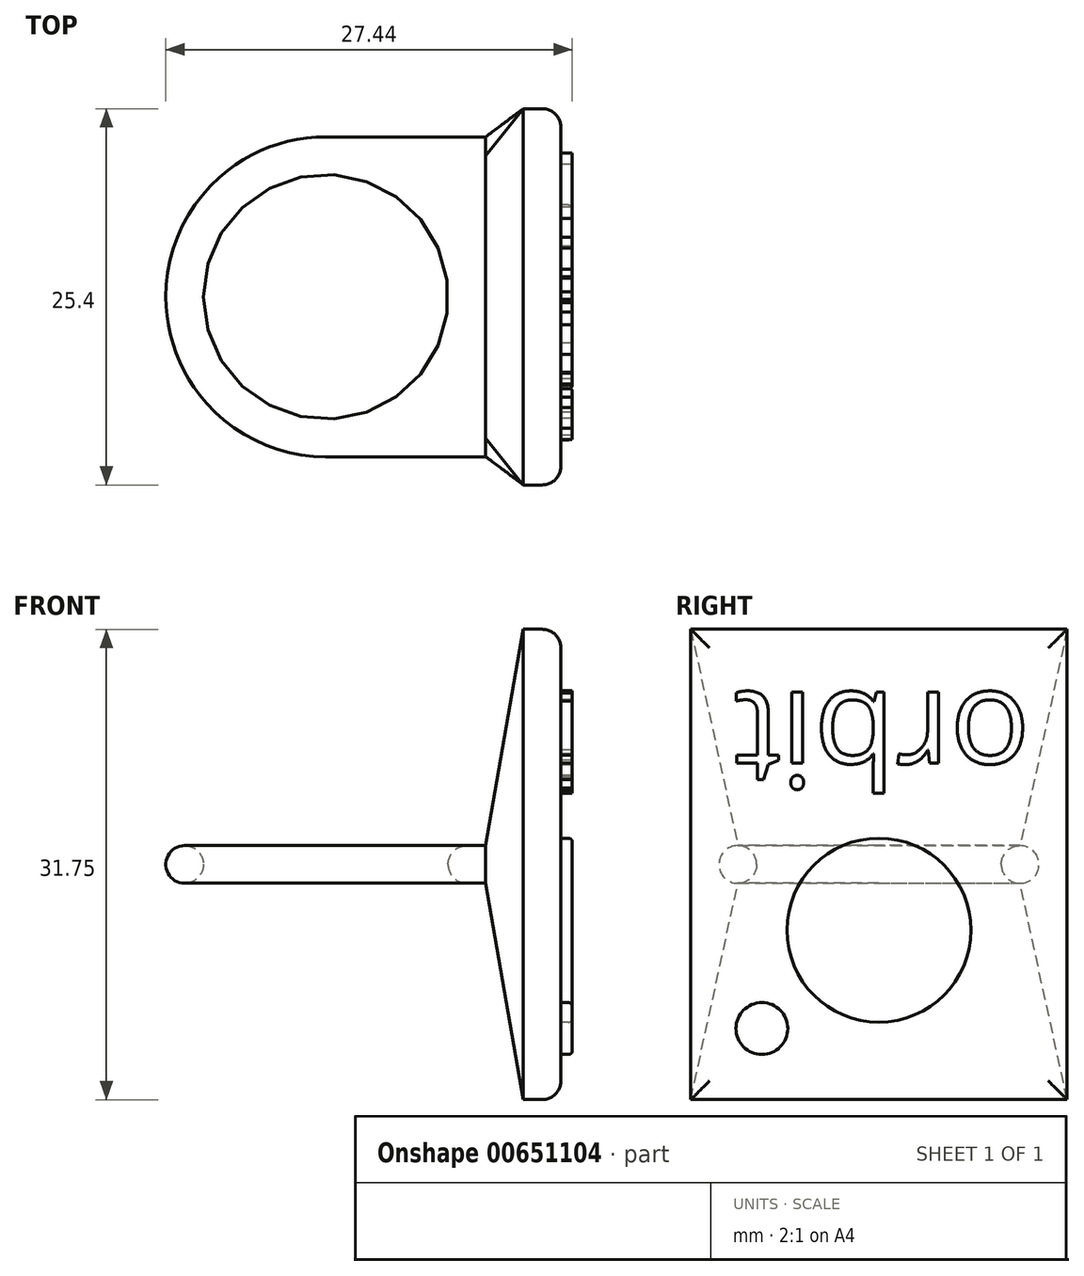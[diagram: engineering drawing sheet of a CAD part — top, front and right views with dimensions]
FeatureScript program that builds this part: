
annotation { "Feature Type Name" : "Feature", "Feature Type Description" : "" }
export const myFeature = defineFeature(function(context is Context, id is Id, definition is map)
    precondition{}
    {
        {
            var Q0;
            Q0=qCreatedBy(makeId("Top.planeOp"),FACE);
            var sketch = newSketch(context, id + "F0", { "sketchPlane" : qUnion([Q0])});
            skCircle(sketch, "E0", {"center": v(0, 0) * mm, "radius": 8.26 * mm});
            skCircle(sketch, "E1.0", {"center": v(0, 0) * mm, "radius": 10.8 * mm});
            skLineSegment(sketch, "E2", {"start": v(0, -10.8) * mm, "end": v(28.84, -10.8) * mm});
            skLineSegment(sketch, "E3", {"start": v(0, 10.8) * mm, "end": v(27.85, 10.8) * mm});
            skLineSegment(sketch, "E4", {"start": v(10.8, 0) * mm, "end": v(10.8, 10.8) * mm});
            skLineSegment(sketch, "E5", {"start": v(10.8, 10.8) * mm, "end": v(10.8, -10.8) * mm});
            skSolve(sketch);
        }
        {
            var Q0;
            Q0=qSketchRegion(id+"F0",true);
            extrude(context, id + "F1", {"entities" : qUnion([Q0]), "depth" : 2.54 * mm, "offsetDistance" : 25.4 * mm});
        }
        {
            var Q0;
            Q0=makeQuery(id+"F1.opExtrude","CAP_EDGE",EDGE,{"disambiguationData":[OSD([sQuery(id+"F0.wireOp",EDGE,"E0")])],"isStart":false});
            var Q1;
            Q1=makeQuery(id+"F1.opExtrude","CAP_EDGE",EDGE,{"disambiguationData":[OSD([sQuery(id+"F0.wireOp",EDGE,"E0")])],"isStart":true});
            var Q2;
            Q2=makeQuery(id+"F1.opExtrude","CAP_EDGE",EDGE,{"disambiguationData":[OSD([sQuery(id+"F0.wireOp",EDGE,"E1.0")])],"isStart":false});
            var Q3;
            Q3=makeQuery(id+"F1.opExtrude","CAP_EDGE",EDGE,{"disambiguationData":[OSD([sQuery(id+"F0.wireOp",EDGE,"E1.0")])],"isStart":true});
            fillet(context, id + "F2", {"entities" : qUnion([Q0, Q1, Q2, Q3]), "radius" : 1.27 * mm, "tangentPropagation" : true, "allowEdgeOverflow" : false});
        }
        {
            var Q0;
            Q0=makeQuery(id+"F1.opExtrude","SWEPT_FACE",FACE,{"disambiguationData":[OSD([sQuery(id+"F0.wireOp",EDGE,"E5")])]});
            cPlane(context, id + "F3", {"entities" : qUnion([Q0]), "cplaneType" : CPlaneType.OFFSET, "offset" : 2.54 * mm, "width" : 152.4 * mm, "height" : 152.4 * mm});
        }
        {
            var Q0;
            Q0=qCreatedBy(id+"F3.planeOp",FACE);
            var sketch = newSketch(context, id + "F4", { "sketchPlane" : qUnion([Q0])});
            skLineSegment(sketch, "E6", {"start": v(0, 0) * mm, "end": v(0, 2.54) * mm});
            skLineSegment(sketch, "E7.bottom", {"start": v(-12.7, 17.15) * mm, "end": v(12.7, 17.15) * mm});
            skLineSegment(sketch, "E7.top", {"start": v(-12.7, -14.6) * mm, "end": v(12.7, -14.6) * mm});
            skLineSegment(sketch, "E7.left", {"start": v(-12.7, 17.15) * mm, "end": v(-12.7, -14.6) * mm});
            skLineSegment(sketch, "E7.right", {"start": v(12.7, 17.15) * mm, "end": v(12.7, -14.6) * mm});
            skPoint(sketch, "E7.middle", {"position": v(0, 1.27) * mm});
            skSolve(sketch);
        }
        {
            var Q0;
            Q0 = qSketchRegion(id + "F4", true);
            extrude(context, id + "F5", {"entities" : qUnion([Q0]), "depth" : 2.54 * mm, "offsetDistance" : 25.4 * mm});
        }
        {
            var Q0;
            Q0=makeQuery(id+"F5.opExtrude","CAP_FACE",FACE,{"disambiguationData":[OSD([sQuery(id+"F4.wireOp",EDGE,"E7.bottom"),sQuery(id+"F4.wireOp",EDGE,"E7.top"),sQuery(id+"F4.wireOp",EDGE,"E7.left"),sQuery(id+"F4.wireOp",EDGE,"E7.right")])],"isStart":true});
            var Q1;
            Q1=makeQuery(id+"F1.opExtrude","SWEPT_FACE",FACE,{"disambiguationData":[OSD([sQuery(id+"F0.wireOp",EDGE,"E5")])]});
            loft(context, id + "F6", {"sheetProfilesArray" : [{ "sheetProfileEntities" : qUnion([Q0]) }, { "sheetProfileEntities" : qUnion([Q1]) }]});
        }
        {
            var Q0;
            Q0=makeQuery(id+"F5.opExtrude","CAP_EDGE",EDGE,{"disambiguationData":[OSD([sQuery(id+"F4.wireOp",EDGE,"E7.right")])],"isStart":false});
            var Q1;
            Q1=makeQuery(id+"F5.opExtrude","CAP_EDGE",EDGE,{"disambiguationData":[OSD([sQuery(id+"F4.wireOp",EDGE,"E7.bottom")])],"isStart":false});
            var Q2;
            Q2=makeQuery(id+"F5.opExtrude","CAP_EDGE",EDGE,{"disambiguationData":[OSD([sQuery(id+"F4.wireOp",EDGE,"E7.top")])],"isStart":false});
            var Q3;
            Q3=makeQuery(id+"F5.opExtrude","CAP_EDGE",EDGE,{"disambiguationData":[OSD([sQuery(id+"F4.wireOp",EDGE,"E7.left")])],"isStart":false});
            fillet(context, id + "F7", {"entities" : qUnion([Q0, Q1, Q2, Q3]), "radius" : 1.27 * mm, "tangentPropagation" : true, "allowEdgeOverflow" : false});
        }
        {
            var Q0;
            Q0=makeQuery(id+"F5.opExtrude","CAP_FACE",FACE,{"disambiguationData":[OSD([sQuery(id+"F4.wireOp",EDGE,"E7.bottom"),sQuery(id+"F4.wireOp",EDGE,"E7.top"),sQuery(id+"F4.wireOp",EDGE,"E7.left"),sQuery(id+"F4.wireOp",EDGE,"E7.right")])],"isStart":false});
            var sketch = newSketch(context, id + "F8", { "sketchPlane" : qUnion([Q0])});
            skLineSegment(sketch, "E8", {"start": v(0, -13.34) * mm, "end": v(0, 15.88) * mm});
            skCircle(sketch, "E9", {"center": v(0, -3.17) * mm, "radius": 6.2 * mm});
            skCircle(sketch, "E10", {"center": v(-7.9, -9.8) * mm, "radius": 1.75 * mm});
            skSolve(sketch);
        }
        {
            var Q0;
            Q0 = qSketchRegion(id + "F8", true);
            extrude(context, id + "F9", {"entities" : qUnion([Q0]), "operationType" : NewBodyOperationType.ADD, "depth" : 0.76 * mm, "offsetDistance" : 25.4 * mm});
        }
        {
            var Q0;
            Q0=makeQuery(id+"F5.opExtrude","CAP_FACE",FACE,{"disambiguationData":[OSD([sQuery(id+"F4.wireOp",EDGE,"E7.bottom"),sQuery(id+"F4.wireOp",EDGE,"E7.top"),sQuery(id+"F4.wireOp",EDGE,"E7.left"),sQuery(id+"F4.wireOp",EDGE,"E7.right")])],"isStart":false});
            var sketch = newSketch(context, id + "F10", { "sketchPlane" : qUnion([Q0])});
            skText(sketch, "E11", { "text": "orbit", "fontName": "OpenSans-Regular.ttf"});
            const initialGuessF10  = {"E11": [0.0102, 0.0129, -1, 0, 0.00646]};
            skSetInitialGuess(sketch, initialGuessF10);
            skSolve(sketch);
        }
        {
            var Q0;
            Q0 = qSketchRegion(id + "F10", true);
            extrude(context, id + "F11", {"entities" : qUnion([Q0]), "operationType" : NewBodyOperationType.ADD, "depth" : 0.76 * mm, "offsetDistance" : 25.4 * mm});
        }
        {
            var Q0;
            Q0=makeQuery(id+"F9.opExtrude","CAP_FACE",FACE,{"disambiguationData":[OSD([sQuery(id+"F8.wireOp",EDGE,"E9")])],"isStart":false});
            var Q1;
            Q1=makeQuery(id+"F9.opExtrude","CAP_FACE",FACE,{"disambiguationData":[OSD([sQuery(id+"F8.wireOp",EDGE,"E10")])],"isStart":false});
            fillet(context, id + "F12", {"entities" : qUnion([Q0, Q1]), "radius" : 0.25 * mm, "tangentPropagation" : true, "allowEdgeOverflow" : false});
        }
    });
